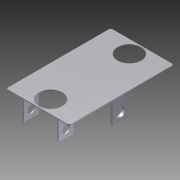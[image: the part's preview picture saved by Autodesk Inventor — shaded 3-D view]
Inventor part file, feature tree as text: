
AUTODESK INVENTOR PART (.ipt)
format: ipt  version: 2011 SP1 (Build 150282100, 282)  size: 144,896 bytes
history: native  units: in
note: dims shown in document units (in); Inventor stores cm internally (conversion verified against a paired STEP export)
features: sketch x11, other x7, extrude x5, hole x4, revolve x2
ambient origin geometry x8: Origin, YZ Plane, XZ Plane, XY Plane, X Axis, Y Axis, Z Axis, Center Point
bodies: Solid1 (feature_tree)
feature tree (29):
  extrude  "Extrusion1"  Depth=0.227in TaperAngle=0.0deg
  extrude  "Extrusion2"  TaperAngle=360.0deg  [1 undecoded]
  extrude  "Extrusion3"  Depth=0.227in TaperAngle=0.0deg
  hole  "Drilling 1"  [1 undecoded]
  hole  "Drilling 2"  [1 undecoded]
  revolve  "Revolution1"  [1 undecoded]
  revolve  "Revolution2"  [1 undecoded]
  extrude  "Extrusion4"  [1 undecoded]
  extrude  "Extrusion5"  [1 undecoded]
  hole  "Drilling 3"  [1 undecoded]
  hole  "Drilling 4"  [1 undecoded]
  other  "to_body_XY"
  other  "to_body_YZ"
  other  "to_body_ZX"
  other  "to_body_X"
  other  "to_body_Y"
  other  "to_body_Z"
  other  "to_body_Center"
  sketch  "Sketch_1"  dims[d0=0.01in d1=0.0in d2=0.227in d3=0.0in]
  sketch  "Sketch_2"  dims[d4=0.227in d5=0.0in]
  sketch  "Sketch_3"  dims[d6=0.079in d7=0.75in d8=0.375in d9=0.25in d10=0.5635in d11=0.012in d12=0.0in]
  sketch  "Sketch4"  dims[d13=0.079in d14=0.75in d15=0.375in d16=0.25in d17=0.5635in d18=0.012in d19=0.0in d20=360.0deg]
  sketch  "Sketch5"  dims[d21=360.0deg d22=0.227in d23=0.0in]
  sketch  "Sketch_12"  dims[d33=0.09in d34=0.75in d35=0.375in d36=0.25in d37=0.5635in d38=0.031in d39=0.0in]
  sketch  "Sketch_13"
  sketch  "Sketch_14"
  sketch  "Sketch_15"
  sketch  "Sketch10"  dims[d24=0.227in d25=0.0in]
  sketch  "Sketch11"  dims[d26=0.09in d27=0.75in d28=0.375in d29=0.25in d30=0.5635in d31=0.031in d32=0.0in]
note: 9 required parameter values undecoded (feature->parameter linkage not recoverable at this tier; creation-order binding heuristic only, values carry confidence <= 0.55)
